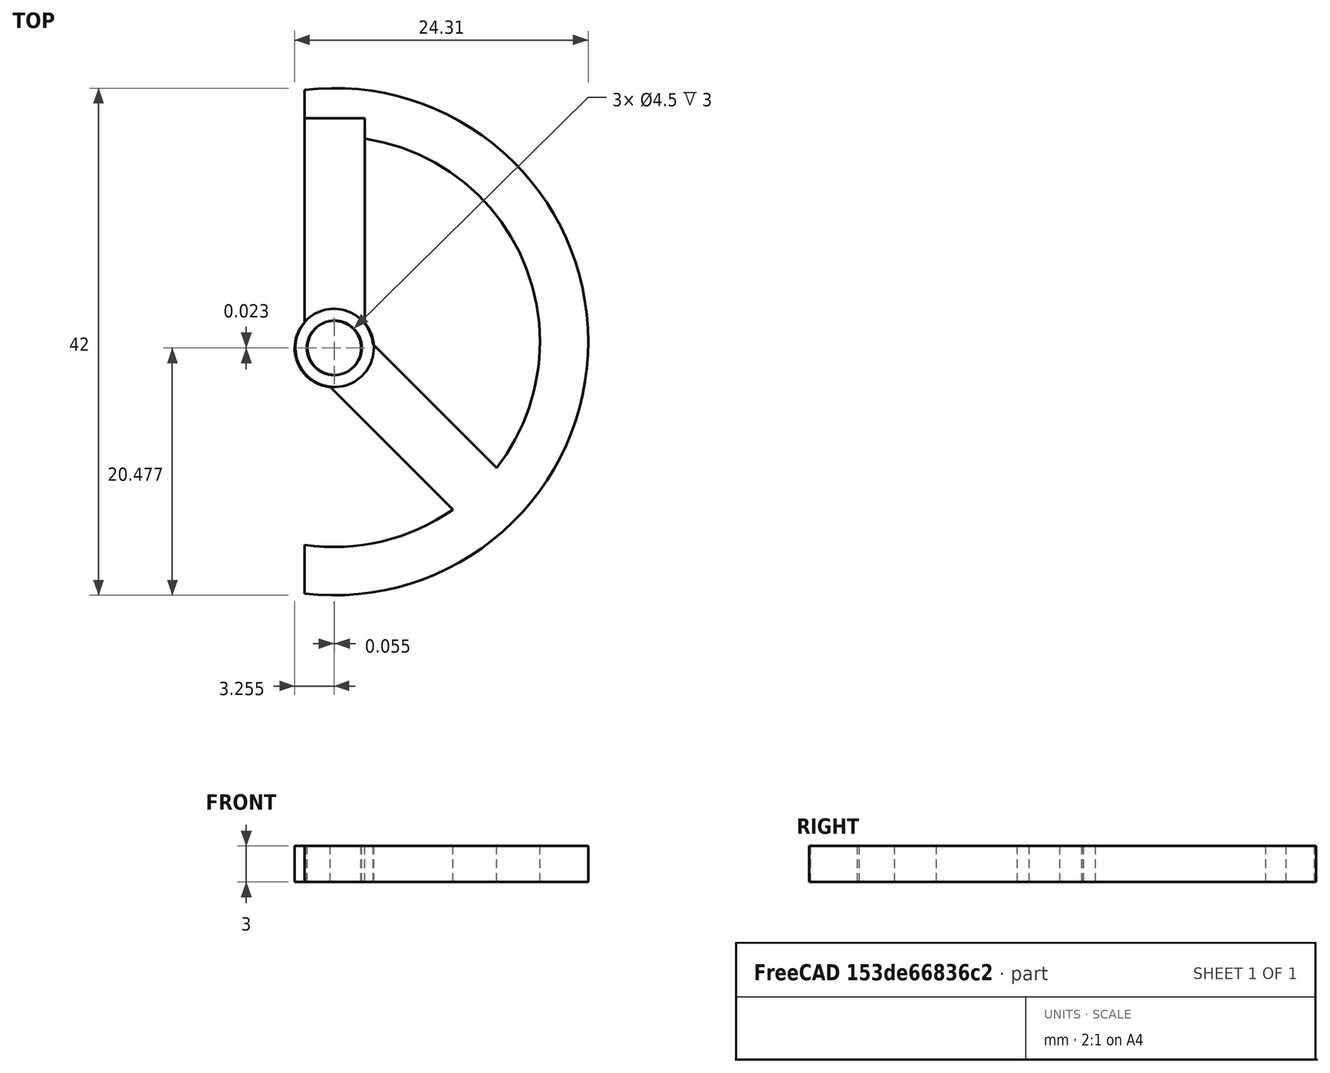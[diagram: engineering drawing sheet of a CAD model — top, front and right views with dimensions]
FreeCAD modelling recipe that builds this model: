
FCSTD DOCUMENT  (FreeCAD 0.19R24366 (Git))
Label: macMiniPowerButtonServoAdapter
License: All rights reserved
LicenseURL: http://en.wikipedia.org/wiki/All_rights_reserved
objects: Part::Box×2, Part::Cylinder×2, Part::FeaturePython×2, Part::Fuse×2, Part::Cut×2
note: 9 computed .brp shape members not serialized (recipe doc carries the construction recipe); baked Part::Feature solids carry a one-line shape summary decoded from their .brp

FEATURE [Part::Box] Box  label="arm"
  AttacherType = Attacher::AttachEngine3D
  Height = 3
  Length = 5
  Placement = pos=(-2.5,-3.5,0) rot=(0,0,1;0rad)
  Width = 19
FEATURE [Part::Cylinder] Cylinder  label="hole"
  Angle = 360
  AttacherType = Attacher::AttachEngine3D
  Height = 3
  Placement = pos=(0,-3.5,0) rot=(0,0,1;0rad)
  Radius = 2.25
FEATURE [Part::FeaturePython] Tube  label="fullCircle"  # WARN: FeaturePython — macro-defined, semantics opaque (R4)
  AttacherType = Attacher::AttachEngine3D
  Height = 3
  InnerRadius = 17
  OuterRadius = 21
  Placement = pos=(0,-3,0) rot=(0,0,1;0rad)
FEATURE [Part::Box] Box001  label="CUTTER"
  AttacherType = Attacher::AttachEngine3D
  Height = 3
  Length = 19
  Placement = pos=(-21.5,-25,0) rot=(0,0,1;0rad)
  Width = 44
FEATURE [Part::Cylinder] Cylinder001  label="frameHole"
  Angle = 360
  AttacherType = Attacher::AttachEngine3D
  Height = 3
  Placement = pos=(0,-3.5,0) rot=(0,0,1;0rad)
  Radius = 3.25
FEATURE [Part::Fuse] Fusion  label="armAndFrameHole"
  Base = -> Box
  Tool = -> Cylinder001
FEATURE [Part::Cut] Cut  label="armHoled"
  Base = -> Fusion
  Tool = -> Cylinder
FEATURE [Part::Cut] Cut001  label="halfCircle"
  Base = -> Tube
  Tool = -> Box001
FEATURE [Part::FeaturePython] Array  label="axels"  # Draft array (typed FeaturePython)
  Angle = 225
  ArrayType = 1
  Axis = (0,0,1)
  Base = -> Cut
  Center = (-0.03223,-3.5,0)
  Count = 2
  ExpandArray = false
  Fuse = false
  IntervalAxis = (0,0,0)
  IntervalX = (50,0,0)
  IntervalY = (0,50,0)
  IntervalZ = (0,0,50)
  NumberCircles = 3
  NumberPolar = 2
  NumberX = 2
  NumberY = 2
  NumberZ = 1
  PlacementList = 2 placements: [(0,0,0),(2.41985,-5.99766,0)]
  RadialDistance = 50
  ScaleList = (2) [(1,1,1),(1,1,1)]
  Symmetry = 1
  TangentialDistance = 25
FEATURE [Part::Fuse] Fusion001  label="macMiniPowerButtonServoAdapter"
  Base = -> Cut001
  Tool = -> Array
